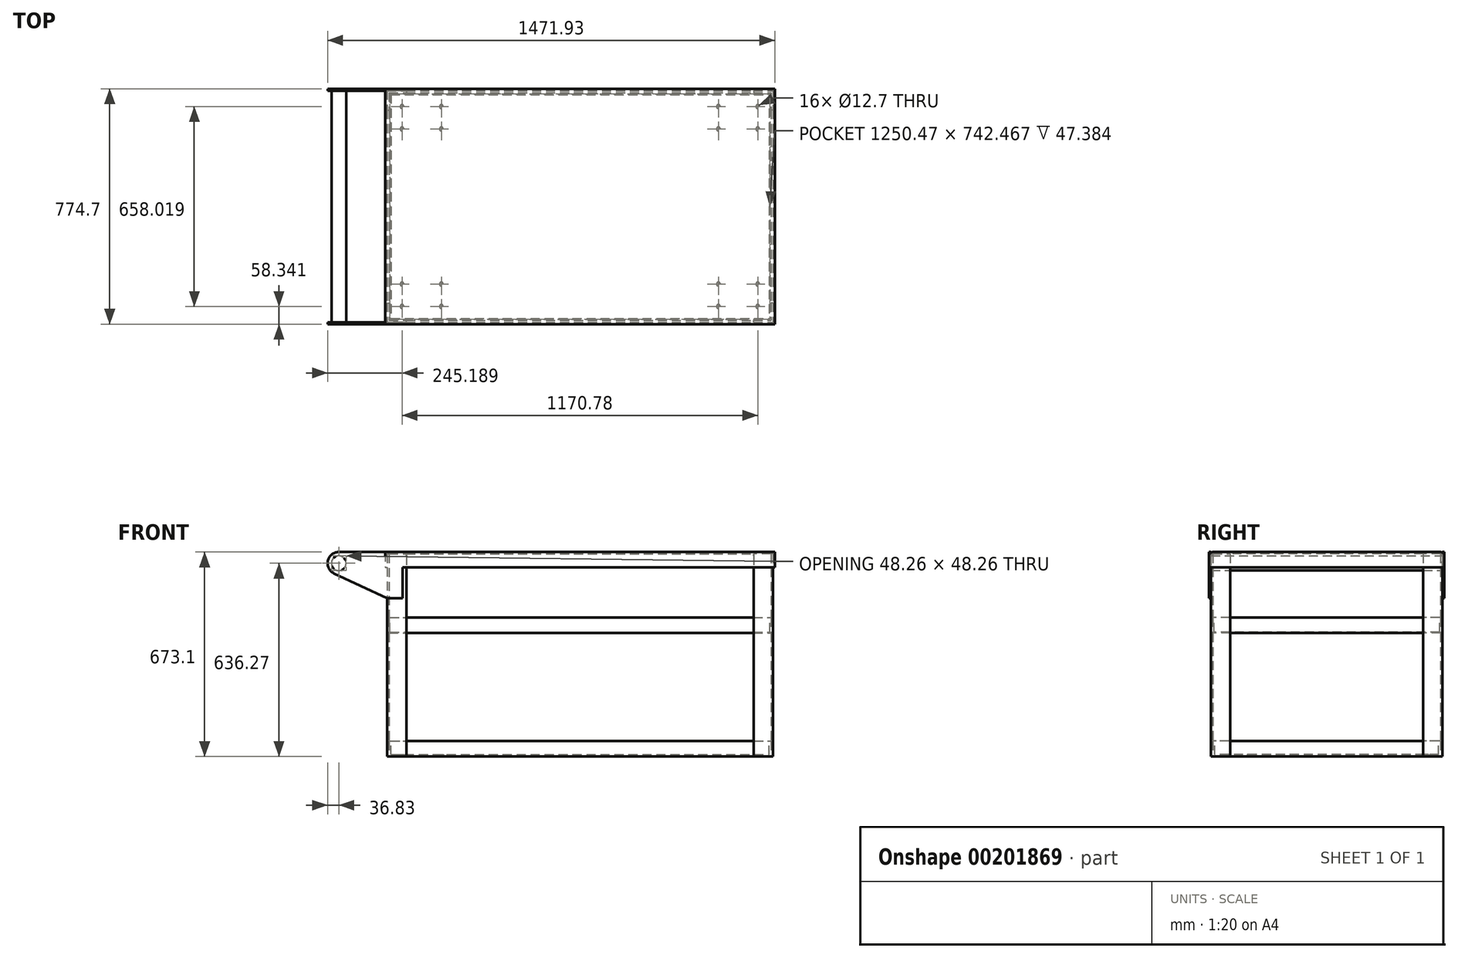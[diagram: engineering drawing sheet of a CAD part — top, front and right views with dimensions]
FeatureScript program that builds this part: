
annotation { "Feature Type Name" : "Feature", "Feature Type Description" : "" }
export const myFeature = defineFeature(function(context is Context, id is Id, definition is map)
    precondition{}
    {
        {
            var Q0;
            Q0=qCreatedBy(makeId("Top.planeOp"),FACE);
            var sketch = newSketch(context, id + "F0", { "sketchPlane" : qUnion([Q0])});
            skLineSegment(sketch, "E0.bottom", {"start": v(-635, 381) * mm, "end": v(635, 381) * mm, "construction": true});
            skLineSegment(sketch, "E0.top", {"start": v(-635, -381) * mm, "end": v(635, -381) * mm, "construction": true});
            skLineSegment(sketch, "E0.left", {"start": v(-635, 381) * mm, "end": v(-635, -381) * mm, "construction": true});
            skLineSegment(sketch, "E0.right", {"start": v(635, 381) * mm, "end": v(635, -381) * mm, "construction": true});
            skPoint(sketch, "E0.middle", {"position": v(0, 0) * mm});
            skLineSegment(sketch, "E1.top", {"start": v(-635, 317.5) * mm, "end": v(-628.65, 317.5) * mm});
            skLineSegment(sketch, "E1.left", {"start": v(-635, 381) * mm, "end": v(-635, 317.5) * mm});
            skLineSegment(sketch, "E1.right", {"start": v(-628.65, 374.65) * mm, "end": v(-628.65, 317.5) * mm});
            skLineSegment(sketch, "E2.top", {"start": v(-628.65, 374.65) * mm, "end": v(-571.5, 374.65) * mm});
            skLineSegment(sketch, "E2.right", {"start": v(-571.5, 381) * mm, "end": v(-571.5, 374.65) * mm});
            skLineSegment(sketch, "E3", {"start": v(0, 381) * mm, "end": v(0, 0) * mm, "construction": true});
            skLineSegment(sketch, "E4", {"start": v(-635, 0) * mm, "end": v(0, 0) * mm, "construction": true});
            skLineSegment(sketch, "E5", {"start": v(-635, 381) * mm, "end": v(-571.5, 381) * mm});
            skLineSegment(sketch, "E6.MirrorCS", {"start": v(635, 317.5) * mm, "end": v(628.65, 317.5) * mm});
            skLineSegment(sketch, "E7.MirrorCS", {"start": v(571.5, 381) * mm, "end": v(571.5, 374.65) * mm});
            skLineSegment(sketch, "E8.MirrorCS", {"start": v(635, 381) * mm, "end": v(571.5, 381) * mm});
            skLineSegment(sketch, "E9.MirrorCS", {"start": v(628.65, 374.65) * mm, "end": v(628.65, 317.5) * mm});
            skLineSegment(sketch, "E10.MirrorCS", {"start": v(628.65, 374.65) * mm, "end": v(571.5, 374.65) * mm});
            skLineSegment(sketch, "E11.MirrorCS", {"start": v(635, 381) * mm, "end": v(635, 317.5) * mm});
            skLineSegment(sketch, "E12.MirrorCS", {"start": v(635, -317.5) * mm, "end": v(628.65, -317.5) * mm});
            skLineSegment(sketch, "E13.MirrorCS", {"start": v(-571.5, -381) * mm, "end": v(-571.5, -374.65) * mm});
            skLineSegment(sketch, "E14.MirrorCS", {"start": v(-635, -317.5) * mm, "end": v(-628.65, -317.5) * mm});
            skLineSegment(sketch, "E15.MirrorCS", {"start": v(571.5, -381) * mm, "end": v(571.5, -374.65) * mm});
            skLineSegment(sketch, "E16.MirrorCS", {"start": v(628.65, -374.65) * mm, "end": v(571.5, -374.65) * mm});
            skLineSegment(sketch, "E17.MirrorCS", {"start": v(-635, -381) * mm, "end": v(-571.5, -381) * mm});
            skLineSegment(sketch, "E18.MirrorCS", {"start": v(-628.65, -374.65) * mm, "end": v(-571.5, -374.65) * mm});
            skLineSegment(sketch, "E19.MirrorCS", {"start": v(-628.65, -374.65) * mm, "end": v(-628.65, -317.5) * mm});
            skLineSegment(sketch, "E20.MirrorCS", {"start": v(635, -381) * mm, "end": v(571.5, -381) * mm});
            skLineSegment(sketch, "E21.MirrorCS", {"start": v(-635, -381) * mm, "end": v(-635, -317.5) * mm});
            skLineSegment(sketch, "E22.MirrorCS", {"start": v(635, -381) * mm, "end": v(635, -317.5) * mm});
            skLineSegment(sketch, "E23.MirrorCS", {"start": v(628.65, -374.65) * mm, "end": v(628.65, -317.5) * mm});
            skSolve(sketch);
        }
        {
            var Q0;
            Q0 = qSketchRegion(id + "F0", true);
            extrude(context, id + "F1", {"entities" : qUnion([Q0]), "depth" : 666.75 * mm});
        }
        {
            var Q0;
            Q0=qCreatedBy(makeId("Front.planeOp"),FACE);
            var sketch = newSketch(context, id + "F2", { "sketchPlane" : qUnion([Q0])});
            skLineSegment(sketch, "E24.bottom", {"start": v(-628.65, 0) * mm, "end": v(628.65, 0) * mm});
            skLineSegment(sketch, "E24.top", {"start": v(-628.65, 50.8) * mm, "end": v(628.65, 50.8) * mm});
            skLineSegment(sketch, "E24.left", {"start": v(-628.65, 0) * mm, "end": v(-628.65, 50.8) * mm});
            skLineSegment(sketch, "E24.right", {"start": v(628.65, 0) * mm, "end": v(628.65, 50.8) * mm});
            skLineSegment(sketch, "E25.bottom", {"start": v(-628.65, 406.4) * mm, "end": v(628.65, 406.4) * mm});
            skLineSegment(sketch, "E25.top", {"start": v(-628.65, 457.2) * mm, "end": v(628.65, 457.2) * mm});
            skLineSegment(sketch, "E25.left", {"start": v(-628.65, 406.4) * mm, "end": v(-628.65, 457.2) * mm});
            skLineSegment(sketch, "E25.right", {"start": v(628.65, 406.4) * mm, "end": v(628.65, 457.2) * mm});
            skSolve(sketch);
        }
        {
            var Q0;
            Q0 = qSketchRegion(id + "F2", true);
            var Q1;
            Q1=makeQuery(id+"F1.opExtrude","SWEPT_FACE",FACE,{"disambiguationData":[OSD([sQuery(id+"F0.wireOp",EDGE,"E2.top")])]});
            var Q2;
            Q2=makeQuery(id+"F1.opExtrude","SWEPT_FACE",FACE,{"disambiguationData":[OSD([sQuery(id+"F0.wireOp",EDGE,"E18.MirrorCS")])]});
            extrude(context, id + "F3", {"entities" : qUnion([Q0]), "endBound" : BoundingType.UP_TO_SURFACE, "oppositeDirection" : true, "endBoundEntityFace" : qUnion([Q1]), "depth" : 25.4 * mm, "hasSecondDirection" : true, "secondDirectionBound" : SecondDirectionBoundingType.UP_TO_SURFACE, "secondDirectionOppositeDirection" : false, "secondDirectionBoundEntityFace" : qUnion([Q2]), "secondDirectionDepth" : 25.4 * mm});
        }
        {
            var Q0;
            Q0=makeQuery(id+"F1.opExtrude","CAP_FACE",FACE,{"disambiguationData":[OSD([sQuery(id+"F0.wireOp",EDGE,"E1.top"),sQuery(id+"F0.wireOp",EDGE,"E1.left"),sQuery(id+"F0.wireOp",EDGE,"E1.right"),sQuery(id+"F0.wireOp",EDGE,"E2.top"),sQuery(id+"F0.wireOp",EDGE,"E2.right"),sQuery(id+"F0.wireOp",EDGE,"E5")])],"isStart":false});
            var sketch = newSketch(context, id + "F4", { "sketchPlane" : qUnion([Q0])});
            skLineSegment(sketch, "E26.bottom", {"start": v(-641.35, 387.35) * mm, "end": v(641.35, 387.35) * mm});
            skLineSegment(sketch, "E26.top", {"start": v(-641.35, -387.35) * mm, "end": v(641.35, -387.35) * mm});
            skLineSegment(sketch, "E26.left", {"start": v(-641.35, 387.35) * mm, "end": v(-641.35, -387.35) * mm});
            skLineSegment(sketch, "E26.right", {"start": v(641.35, 387.35) * mm, "end": v(641.35, -387.35) * mm});
            skPoint(sketch, "E26.middle", {"position": v(0, 0) * mm});
            skLineSegment(sketch, "E27.bottom", {"start": v(-641.35, 387.35) * mm, "end": v(-635, 387.35) * mm, "construction": true});
            skLineSegment(sketch, "E27.top", {"start": v(-641.35, 381) * mm, "end": v(-635, 381) * mm, "construction": true});
            skLineSegment(sketch, "E27.left", {"start": v(-641.35, 387.35) * mm, "end": v(-641.35, 381) * mm, "construction": true});
            skLineSegment(sketch, "E27.right", {"start": v(-635, 387.35) * mm, "end": v(-635, 381) * mm, "construction": true});
            skSolve(sketch);
        }
        {
            var Q0;
            Q0 = qSketchRegion(id + "F4", true);
            extrude(context, id + "F5", {"entities" : qUnion([Q0]), "oppositeDirection" : true, "depth" : 44.45 * mm, "hasSecondDirection" : true, "secondDirectionOppositeDirection" : false, "secondDirectionDepth" : 6.35 * mm});
        }
        {
            var Q0;
            Q0=makeQuery(id+"F5.opExtrude","CAP_EDGE",EDGE,{"disambiguationData":[OSD([sQuery(id+"F4.wireOp",EDGE,"E26.top")])],"isStart":true});
            var Q1;
            Q1=makeQuery(id+"F5.opExtrude","CAP_EDGE",EDGE,{"disambiguationData":[OSD([sQuery(id+"F4.wireOp",EDGE,"E26.bottom")])],"isStart":true});
            var Q2;
            Q2=makeQuery(id+"F3.opExtrude","TWEAK_EDGE",EDGE,{"derivedFrom":[makeQuery(id+"F1.opExtrude","SWEPT_FACE",FACE,{"disambiguationData":[OSD([sQuery(id+"F0.wireOp",EDGE,"E18.MirrorCS")])]}),makeQuery(id+"F2.imprint","IMPRINT",EDGE,{"derivedFrom":sQuery(id+"F2.wireOp",EDGE,"E25.bottom")})]});
            var Q3;
            Q3=makeQuery(id+"F3.opExtrude","TWEAK_EDGE",EDGE,{"derivedFrom":[makeQuery(id+"F1.opExtrude","SWEPT_FACE",FACE,{"disambiguationData":[OSD([sQuery(id+"F0.wireOp",EDGE,"E18.MirrorCS")])]}),makeQuery(id+"F2.imprint","IMPRINT",EDGE,{"derivedFrom":sQuery(id+"F2.wireOp",EDGE,"E24.bottom")})]});
            var Q4;
            Q4=makeQuery(id+"F3.opExtrude","TWEAK_EDGE",EDGE,{"derivedFrom":[makeQuery(id+"F1.opExtrude","SWEPT_FACE",FACE,{"disambiguationData":[OSD([sQuery(id+"F0.wireOp",EDGE,"E2.top")])]}),makeQuery(id+"F2.imprint","IMPRINT",EDGE,{"derivedFrom":sQuery(id+"F2.wireOp",EDGE,"E25.bottom")})]});
            var Q5;
            Q5=makeQuery(id+"F3.opExtrude","TWEAK_EDGE",EDGE,{"derivedFrom":[makeQuery(id+"F1.opExtrude","SWEPT_FACE",FACE,{"disambiguationData":[OSD([sQuery(id+"F0.wireOp",EDGE,"E2.top")])]}),makeQuery(id+"F2.imprint","IMPRINT",EDGE,{"derivedFrom":sQuery(id+"F2.wireOp",EDGE,"E24.bottom")})]});
            fillet(context, id + "F6", {"entities" : qUnion([Q0, Q1, Q2, Q3, Q4, Q5]), "radius" : 12.7 * mm, "tangentPropagation" : true, "allowEdgeOverflow" : false});
        }
        {
            var Q0;
            Q0=makeQuery(id+"F5.opExtrude","CAP_FACE",FACE,{"disambiguationData":[OSD([sQuery(id+"F4.wireOp",EDGE,"E26.bottom"),sQuery(id+"F4.wireOp",EDGE,"E26.top"),sQuery(id+"F4.wireOp",EDGE,"E26.left"),sQuery(id+"F4.wireOp",EDGE,"E26.right")])],"isStart":false});
            var Q1;
            Q1=makeQuery(id+"F3.opExtrude","SWEPT_FACE",FACE,{"disambiguationData":[OSD([sQuery(id+"F2.wireOp",EDGE,"E24.top")])]});
            shell(context, id + "F7", {"entities" : qUnion([Q0, Q1]), "thickness" : 6.35 * mm});
        }
        {
            var Q0;
            Q0=makeQuery(id+"F3.opExtrude","SWEPT_FACE",FACE,{"disambiguationData":[OSD([sQuery(id+"F2.wireOp",EDGE,"E25.top")])]});
            shell(context, id + "F8", {"entities" : qUnion([Q0]), "thickness" : 3.42 * mm});
        }
        {
            var Q0;
            Q0=makeQuery(id+"F3.opExtrude","SWEPT_BODY",BODY,{"disambiguationData":[OSD([sQuery(id+"F2.wireOp",EDGE,"E25.bottom"),sQuery(id+"F2.wireOp",EDGE,"E25.top"),sQuery(id+"F2.wireOp",EDGE,"E25.left"),sQuery(id+"F2.wireOp",EDGE,"E25.right")])]});
            var Q1;
            Q1=makeQuery(id+"F3.opExtrude","SWEPT_BODY",BODY,{"disambiguationData":[OSD([sQuery(id+"F2.wireOp",EDGE,"E24.bottom"),sQuery(id+"F2.wireOp",EDGE,"E24.top"),sQuery(id+"F2.wireOp",EDGE,"E24.left"),sQuery(id+"F2.wireOp",EDGE,"E24.right")])]});
            var Q2;
            Q2=makeQuery(id+"F5.opExtrude","SWEPT_BODY",BODY,{"disambiguationData":[OSD([sQuery(id+"F4.wireOp",EDGE,"E26.bottom"),sQuery(id+"F4.wireOp",EDGE,"E26.top"),sQuery(id+"F4.wireOp",EDGE,"E26.left"),sQuery(id+"F4.wireOp",EDGE,"E26.right")])]});
            var Q3;
            Q3=makeQuery(id+"F1.opExtrude","SWEPT_BODY",BODY,{"disambiguationData":[OSD([sQuery(id+"F0.wireOp",EDGE,"E13.MirrorCS"),sQuery(id+"F0.wireOp",EDGE,"E14.MirrorCS"),sQuery(id+"F0.wireOp",EDGE,"E17.MirrorCS"),sQuery(id+"F0.wireOp",EDGE,"E18.MirrorCS"),sQuery(id+"F0.wireOp",EDGE,"E19.MirrorCS"),sQuery(id+"F0.wireOp",EDGE,"E21.MirrorCS")])]});
            var Q4;
            Q4=makeQuery(id+"F1.opExtrude","SWEPT_BODY",BODY,{"disambiguationData":[OSD([sQuery(id+"F0.wireOp",EDGE,"E12.MirrorCS"),sQuery(id+"F0.wireOp",EDGE,"E15.MirrorCS"),sQuery(id+"F0.wireOp",EDGE,"E16.MirrorCS"),sQuery(id+"F0.wireOp",EDGE,"E20.MirrorCS"),sQuery(id+"F0.wireOp",EDGE,"E22.MirrorCS"),sQuery(id+"F0.wireOp",EDGE,"E23.MirrorCS")])]});
            var Q5;
            Q5=makeQuery(id+"F1.opExtrude","SWEPT_BODY",BODY,{"disambiguationData":[OSD([sQuery(id+"F0.wireOp",EDGE,"E6.MirrorCS"),sQuery(id+"F0.wireOp",EDGE,"E7.MirrorCS"),sQuery(id+"F0.wireOp",EDGE,"E8.MirrorCS"),sQuery(id+"F0.wireOp",EDGE,"E9.MirrorCS"),sQuery(id+"F0.wireOp",EDGE,"E10.MirrorCS"),sQuery(id+"F0.wireOp",EDGE,"E11.MirrorCS")])]});
            var Q6;
            Q6=makeQuery(id+"F1.opExtrude","SWEPT_BODY",BODY,{"disambiguationData":[OSD([sQuery(id+"F0.wireOp",EDGE,"E1.top"),sQuery(id+"F0.wireOp",EDGE,"E1.left"),sQuery(id+"F0.wireOp",EDGE,"E1.right"),sQuery(id+"F0.wireOp",EDGE,"E2.top"),sQuery(id+"F0.wireOp",EDGE,"E2.right"),sQuery(id+"F0.wireOp",EDGE,"E5")])]});
            booleanBodies(context, id + "F9", {"operationType" : BooleanOperationType.UNION, "tools" : qUnion([Q0, Q1, Q2, Q3, Q4, Q5, Q6])});
        }
        {
            var Q0;
            Q0=makeQuery(id+"F1.opExtrude","SWEPT_FACE",FACE,{"disambiguationData":[OSD([sQuery(id+"F0.wireOp",EDGE,"E17.MirrorCS")])]});
            var sketch = newSketch(context, id + "F10", { "sketchPlane" : qUnion([Q0])});
            skLineSegment(sketch, "E28", {"start": v(-641.35, 622.3) * mm, "end": v(-584.2, 622.3) * mm});
            skLineSegment(sketch, "E29", {"start": v(-584.2, 622.3) * mm, "end": v(-584.2, 520.7) * mm});
            skLineSegment(sketch, "E30", {"start": v(-584.2, 520.7) * mm, "end": v(-635, 520.7) * mm});
            skLineSegment(sketch, "E31", {"start": v(-635, 520.7) * mm, "end": v(-809.46, 602.96) * mm});
            skLineSegment(sketch, "E32", {"start": v(-793.75, 673.1) * mm, "end": v(-641.35, 673.1) * mm});
            skArc(sketch, "E33", {"start": v(-793.75, 673.1) * mm, "mid": v(-829.69, 644.32) * mm, "end": v(-809.46, 602.96) * mm});
            skLineSegment(sketch, "E34", {"start": v(-641.35, 673.1) * mm, "end": v(-641.35, 622.3) * mm});
            skCircle(sketch, "E35", {"center": v(-793.75, 636.27) * mm, "radius": 24.13 * mm});
            skSolve(sketch);
        }
        {
            var Q0;
            Q0 = qSketchRegion(id + "F10", true);
            extrude(context, id + "F11", {"entities" : qUnion([Q0]), "depth" : 6.35 * mm});
        }
        {
            var Q0;
            Q0=makeQuery(id+"F11.opExtrude","SWEPT_BODY",BODY,{"disambiguationData":[OSD([sQuery(id+"F10.wireOp",EDGE,"E28"),sQuery(id+"F10.wireOp",EDGE,"E29"),sQuery(id+"F10.wireOp",EDGE,"E30"),sQuery(id+"F10.wireOp",EDGE,"E31"),sQuery(id+"F10.wireOp",EDGE,"E32"),sQuery(id+"F10.wireOp",EDGE,"E33"),sQuery(id+"F10.wireOp",EDGE,"E34"),sQuery(id+"F10.wireOp",EDGE,"E35")])]});
            var Q1;
            Q1=qCreatedBy(makeId("Front.planeOp"),FACE);
            mirror(context, id + "F12", {"operationType" : NewBodyOperationType.ADD, "entities" : qUnion([Q0]), "mirrorPlane" : qUnion([Q1])});
        }
        {
            var Q0;
            Q0=makeQuery(id+"F10.imprint","IMPRINT",FACE,{"disambiguationData":[TD([[makeQuery(id+"F10.imprint","IMPRINT",EDGE,{"derivedFrom":sQuery(id+"F10.wireOp",EDGE,"E35")}),1.0]])]});
            var Q1;
            Q1=makeQuery(id+"F12.boolean.opBoolean","MERGE",FACE,{"derivedFrom":[makeQuery(id+"F5.opExtrude","SWEPT_FACE",FACE,{"disambiguationData":[OSD([sQuery(id+"F4.wireOp",EDGE,"E26.top")])]}),makeQuery(id+"F11.opExtrude","CAP_FACE",FACE,{"disambiguationData":[OSD([sQuery(id+"F10.wireOp",EDGE,"E28"),sQuery(id+"F10.wireOp",EDGE,"E29"),sQuery(id+"F10.wireOp",EDGE,"E30"),sQuery(id+"F10.wireOp",EDGE,"E31"),sQuery(id+"F10.wireOp",EDGE,"E32"),sQuery(id+"F10.wireOp",EDGE,"E33"),sQuery(id+"F10.wireOp",EDGE,"E34"),sQuery(id+"F10.wireOp",EDGE,"E35")])],"isStart":false})]});
            var Q2;
            Q2=makeQuery(id+"F12.boolean.opBoolean","MERGE",FACE,{"derivedFrom":[makeQuery(id+"F5.opExtrude","SWEPT_FACE",FACE,{"disambiguationData":[OSD([sQuery(id+"F4.wireOp",EDGE,"E26.bottom")])]}),makeQuery(id+"F12.opPattern","COPY",FACE,{"derivedFrom":makeQuery(id+"F11.opExtrude","CAP_FACE",FACE,{"disambiguationData":[OSD([sQuery(id+"F10.wireOp",EDGE,"E28"),sQuery(id+"F10.wireOp",EDGE,"E29"),sQuery(id+"F10.wireOp",EDGE,"E30"),sQuery(id+"F10.wireOp",EDGE,"E31"),sQuery(id+"F10.wireOp",EDGE,"E32"),sQuery(id+"F10.wireOp",EDGE,"E33"),sQuery(id+"F10.wireOp",EDGE,"E34"),sQuery(id+"F10.wireOp",EDGE,"E35")])],"isStart":false}),"instanceName":"1"})]});
            extrude(context, id + "F13", {"entities" : qUnion([Q0]), "operationType" : NewBodyOperationType.ADD, "endBound" : BoundingType.UP_TO_SURFACE, "endBoundEntityFace" : qUnion([Q1]), "depth" : 8.9 * mm, "hasSecondDirection" : true, "secondDirectionBound" : SecondDirectionBoundingType.UP_TO_SURFACE, "secondDirectionOppositeDirection" : true, "secondDirectionBoundEntityFace" : qUnion([Q2]), "secondDirectionDepth" : 25.4 * mm});
        }
        {
            var Q0;
            Q0=makeQuery(id+"F9.opBoolean","MERGE",FACE,{"derivedFrom":[makeQuery(id+"F1.opExtrude","CAP_FACE",FACE,{"disambiguationData":[OSD([sQuery(id+"F0.wireOp",EDGE,"E1.top"),sQuery(id+"F0.wireOp",EDGE,"E1.left"),sQuery(id+"F0.wireOp",EDGE,"E1.right"),sQuery(id+"F0.wireOp",EDGE,"E2.top"),sQuery(id+"F0.wireOp",EDGE,"E2.right"),sQuery(id+"F0.wireOp",EDGE,"E5")])],"isStart":true}),makeQuery(id+"F1.opExtrude","CAP_FACE",FACE,{"disambiguationData":[OSD([sQuery(id+"F0.wireOp",EDGE,"E6.MirrorCS"),sQuery(id+"F0.wireOp",EDGE,"E7.MirrorCS"),sQuery(id+"F0.wireOp",EDGE,"E8.MirrorCS"),sQuery(id+"F0.wireOp",EDGE,"E9.MirrorCS"),sQuery(id+"F0.wireOp",EDGE,"E10.MirrorCS"),sQuery(id+"F0.wireOp",EDGE,"E11.MirrorCS")])],"isStart":true}),makeQuery(id+"F1.opExtrude","CAP_FACE",FACE,{"disambiguationData":[OSD([sQuery(id+"F0.wireOp",EDGE,"E12.MirrorCS"),sQuery(id+"F0.wireOp",EDGE,"E15.MirrorCS"),sQuery(id+"F0.wireOp",EDGE,"E16.MirrorCS"),sQuery(id+"F0.wireOp",EDGE,"E20.MirrorCS"),sQuery(id+"F0.wireOp",EDGE,"E22.MirrorCS"),sQuery(id+"F0.wireOp",EDGE,"E23.MirrorCS")])],"isStart":true}),makeQuery(id+"F1.opExtrude","CAP_FACE",FACE,{"disambiguationData":[OSD([sQuery(id+"F0.wireOp",EDGE,"E13.MirrorCS"),sQuery(id+"F0.wireOp",EDGE,"E14.MirrorCS"),sQuery(id+"F0.wireOp",EDGE,"E17.MirrorCS"),sQuery(id+"F0.wireOp",EDGE,"E18.MirrorCS"),sQuery(id+"F0.wireOp",EDGE,"E19.MirrorCS"),sQuery(id+"F0.wireOp",EDGE,"E21.MirrorCS")])],"isStart":true}),makeQuery(id+"F3.opExtrude","SWEPT_FACE",FACE,{"disambiguationData":[OSD([sQuery(id+"F2.wireOp",EDGE,"E24.bottom")])]})]});
            var sketch = newSketch(context, id + "F14", { "sketchPlane" : qUnion([Q0])});
            skLineSegment(sketch, "E36.bottom", {"start": v(444.5, 349.25) * mm, "end": v(596.9, 349.25) * mm, "construction": true});
            skLineSegment(sketch, "E36.top", {"start": v(444.5, 234.95) * mm, "end": v(596.9, 234.95) * mm, "construction": true});
            skLineSegment(sketch, "E36.left", {"start": v(438.15, 342.9) * mm, "end": v(438.15, 241.3) * mm, "construction": true});
            skLineSegment(sketch, "E36.right", {"start": v(603.25, 342.9) * mm, "end": v(603.25, 241.3) * mm, "construction": true});
            skLineSegment(sketch, "E37", {"start": v(438.15, 311.15) * mm, "end": v(476.25, 311.15) * mm, "construction": true});
            skLineSegment(sketch, "E38", {"start": v(476.25, 311.15) * mm, "end": v(476.25, 349.25) * mm, "construction": true});
            skPoint(sketch, "E39.visualSharp", {"position": v(438.15, 234.95) * mm});
            skArc(sketch, "E39.filletArc", {"start": v(438.15, 241.3) * mm, "mid": v(440, 236.8) * mm, "end": v(444.5, 234.95) * mm, "construction": true});
            skPoint(sketch, "E40.visualSharp", {"position": v(603.25, 234.95) * mm});
            skArc(sketch, "E40.filletArc", {"start": v(596.9, 234.95) * mm, "mid": v(601.4, 236.8) * mm, "end": v(603.25, 241.3) * mm, "construction": true});
            skPoint(sketch, "E41.visualSharp", {"position": v(603.25, 349.25) * mm});
            skArc(sketch, "E41.filletArc", {"start": v(603.25, 342.9) * mm, "mid": v(601.4, 347.4) * mm, "end": v(596.9, 349.25) * mm, "construction": true});
            skPoint(sketch, "E42.visualSharp", {"position": v(438.15, 349.25) * mm});
            skArc(sketch, "E42.filletArc", {"start": v(444.5, 349.25) * mm, "mid": v(440, 347.4) * mm, "end": v(438.15, 342.9) * mm, "construction": true});
            skLineSegment(sketch, "E43", {"start": v(520.7, 234.95) * mm, "end": v(520.7, 349.25) * mm, "construction": true});
            skLineSegment(sketch, "E44", {"start": v(438.15, 292.1) * mm, "end": v(603.25, 292.1) * mm, "construction": true});
            skLineSegment(sketch, "E45.bottom", {"start": v(585.4, 255.2) * mm, "end": v(456, 255.2) * mm, "construction": true});
            skLineSegment(sketch, "E45.top", {"start": v(585.4, 329) * mm, "end": v(456, 329) * mm, "construction": true});
            skLineSegment(sketch, "E45.left", {"start": v(585.4, 255.2) * mm, "end": v(585.4, 329) * mm, "construction": true});
            skLineSegment(sketch, "E45.right", {"start": v(456, 255.2) * mm, "end": v(456, 329) * mm, "construction": true});
            skPoint(sketch, "E45.middle", {"position": v(520.7, 292.1) * mm});
            skCircle(sketch, "E46", {"center": v(456, 255.2) * mm, "radius": 6.35 * mm});
            skCircle(sketch, "E47", {"center": v(585.4, 255.2) * mm, "radius": 6.35 * mm});
            skCircle(sketch, "E48", {"center": v(456, 329) * mm, "radius": 6.35 * mm});
            skCircle(sketch, "E49", {"center": v(585.4, 329) * mm, "radius": 6.35 * mm});
            skLineSegment(sketch, "E50", {"start": v(0, 119.29) * mm, "end": v(0, 0) * mm, "construction": true});
            skLineSegment(sketch, "E51", {"start": v(0, 0) * mm, "end": v(102.52, 0) * mm, "construction": true});
            skCircle(sketch, "E52.MirrorC", {"center": v(-585.4, 255.2) * mm, "radius": 6.35 * mm});
            skCircle(sketch, "E53.MirrorC", {"center": v(-456, 255.2) * mm, "radius": 6.35 * mm});
            skCircle(sketch, "E54.MirrorC", {"center": v(-456, 329) * mm, "radius": 6.35 * mm});
            skCircle(sketch, "E55.MirrorC", {"center": v(-585.4, 329) * mm, "radius": 6.35 * mm});
            skCircle(sketch, "E56.MirrorC", {"center": v(585.4, -255.2) * mm, "radius": 6.35 * mm});
            skCircle(sketch, "E57.MirrorC", {"center": v(456, -255.2) * mm, "radius": 6.35 * mm});
            skCircle(sketch, "E58.MirrorC", {"center": v(456, -329) * mm, "radius": 6.35 * mm});
            skCircle(sketch, "E59.MirrorC", {"center": v(585.4, -329) * mm, "radius": 6.35 * mm});
            skCircle(sketch, "E60.MirrorC", {"center": v(-456, -255.2) * mm, "radius": 6.35 * mm});
            skCircle(sketch, "E61.MirrorC", {"center": v(-585.4, -329) * mm, "radius": 6.35 * mm});
            skCircle(sketch, "E62.MirrorC", {"center": v(-585.4, -255.2) * mm, "radius": 6.35 * mm});
            skCircle(sketch, "E63.MirrorC", {"center": v(-456, -329) * mm, "radius": 6.35 * mm});
            skPoint(sketch, "E64.MirrorP", {"position": v(-520.7, 292.1) * mm});
            skPoint(sketch, "E65.MirrorP", {"position": v(520.7, -292.1) * mm});
            skPoint(sketch, "E66.MirrorP", {"position": v(-520.7, -292.1) * mm});
            skSolve(sketch);
        }
        {
            var Q0;
            Q0 = qSketchRegion(id + "F14", true);
            extrude(context, id + "F15", {"entities" : qUnion([Q0]), "operationType" : NewBodyOperationType.REMOVE, "oppositeDirection" : true, "depth" : 25.4 * mm});
        }
    });
